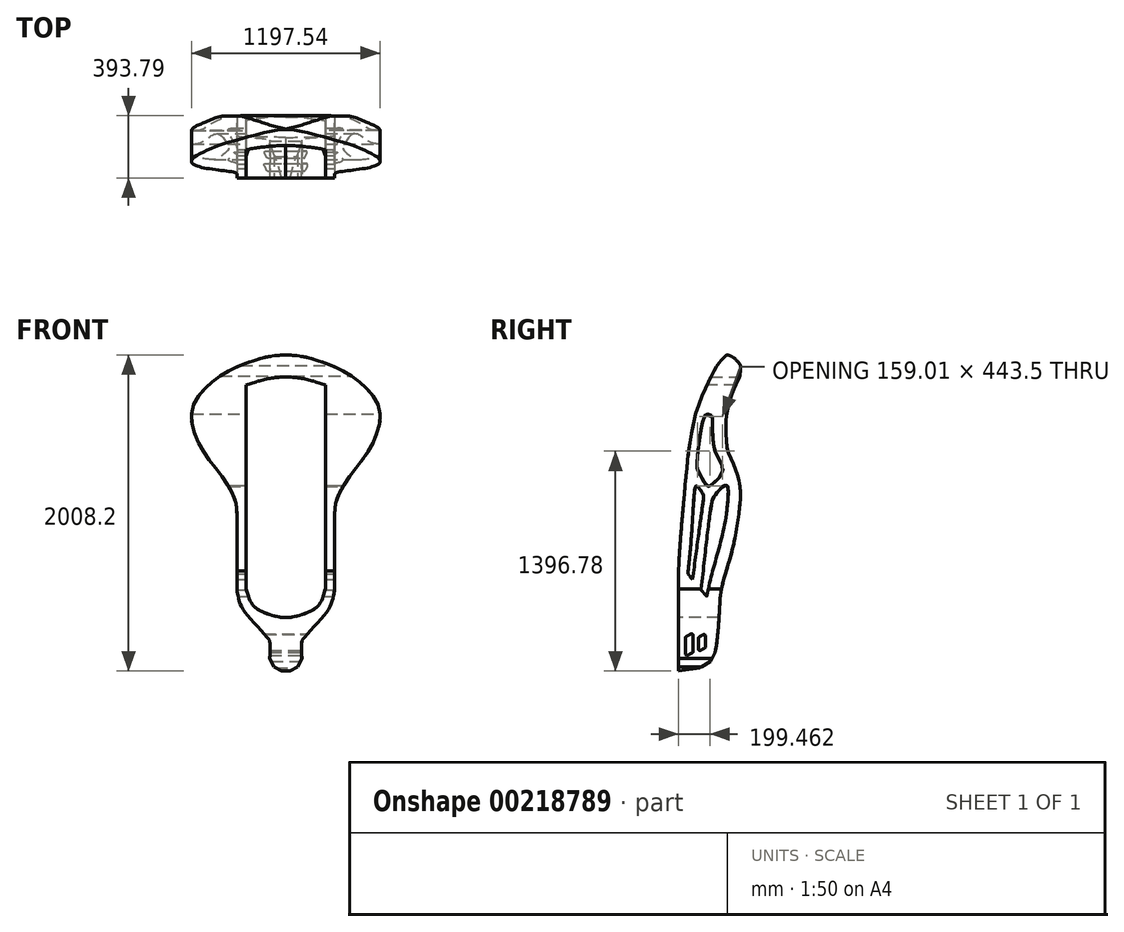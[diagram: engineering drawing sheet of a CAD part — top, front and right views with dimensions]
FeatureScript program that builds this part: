
annotation { "Feature Type Name" : "Feature", "Feature Type Description" : "" }
export const myFeature = defineFeature(function(context is Context, id is Id, definition is map)
    precondition{}
    {
        {
            var Q0;
            Q0=qCreatedBy(makeId("Front.planeOp"),FACE);
            var sketch = newSketch(context, id + "F0", { "sketchPlane" : qUnion([Q0])});
            skLineSegment(sketch, "E0", {"start": v(-255.28, -84.36) * mm, "end": v(252.72, -84.36) * mm});
            skLineSegment(sketch, "E1", {"start": v(0, -829.48) * mm, "end": v(0, 1173.27) * mm});
            skSolve(sketch);
        }
        {
            var Q0;
            Q0=qCreatedBy(makeId("Right.planeOp"),FACE);
            var sketch = newSketch(context, id + "F1", { "sketchPlane" : qUnion([Q0])});
            skLineSegment(sketch, "E2.0", {"start": v(0, -829.48) * mm, "end": v(0, 1173.27) * mm});
            skSolve(sketch);
        }
        {
            var Q0;
            Q0=qCreatedBy(makeId("Front.planeOp"),FACE);
            var sketch = newSketch(context, id + "F2", { "sketchPlane" : qUnion([Q0])});
            skFitSpline(sketch, "E3", {"points": [v(0, 1178.72) * mm, v(-131.61, 1163.15) * mm, v(-387.55, 1062.86) * mm, v(-534.54, 943.54) * mm, v(-586.42, 860.53) * mm, v(-598.52, 786.17) * mm, v(-593.33, 730.83) * mm, v(-536.94, 587.44) * mm, v(-445.29, 459.48) * mm, v(-334.61, 291.74) * mm, v(-310.9, 168.96) * mm], "startDerivative": vector(-1185.5, -55.3) * mm, "endDerivative": vector(0, -1218.83) * mm});
            skLineSegment(sketch, "E4", {"start": v(-310.9, 168.96) * mm, "end": v(-310.9, -308.33) * mm});
            skFitSpline(sketch, "E5", {"points": [v(-310.9, -308.33) * mm, v(-292.5, -393.37) * mm, v(-233.06, -486.5) * mm, v(-109.25, -625.95) * mm, v(-101.61, -641.2) * mm, v(-101.61, -747.96) * mm], "startDerivative": vector(68.26, -452.87) * mm, "endDerivative": vector(-14.07, -627.34) * mm});
            skLineSegment(sketch, "E6", {"start": v(-101.61, -747.96) * mm, "end": v(-75.98, -803.52) * mm});
            skLineSegment(sketch, "E7", {"start": v(-75.98, -803.52) * mm, "end": v(-19.8, -832.39) * mm});
            skLineSegment(sketch, "E8", {"start": v(-19.8, -832.39) * mm, "end": v(0, -832.39) * mm});
            skLineSegment(sketch, "E9", {"start": v(0, 1178.72) * mm, "end": v(0, -832.39) * mm, "construction": true});
            skLineSegment(sketch, "E10.MirrorCS", {"start": v(75.98, -803.52) * mm, "end": v(19.8, -832.39) * mm});
            skLineSegment(sketch, "E11.MirrorCS", {"start": v(101.61, -747.96) * mm, "end": v(75.98, -803.52) * mm});
            skLineSegment(sketch, "E12.MirrorCS", {"start": v(19.8, -832.39) * mm, "end": v(0, -832.39) * mm});
            skFitSpline(sketch, "E13.MirrorCS", {"points": [v(310.9, -308.33) * mm, v(292.5, -393.37) * mm, v(233.06, -486.5) * mm, v(109.25, -625.95) * mm, v(101.61, -641.2) * mm, v(101.61, -747.96) * mm], "startDerivative": vector(-68.26, -452.87) * mm, "endDerivative": vector(14.07, -627.34) * mm});
            skLineSegment(sketch, "E14.MirrorCS", {"start": v(310.9, 168.96) * mm, "end": v(310.9, -308.33) * mm});
            skFitSpline(sketch, "E15.MirrorCS", {"points": [v(0, 1178.72) * mm, v(131.61, 1163.15) * mm, v(387.55, 1062.86) * mm, v(534.54, 943.54) * mm, v(586.42, 860.53) * mm, v(598.52, 786.17) * mm, v(593.33, 730.83) * mm, v(536.94, 587.44) * mm, v(445.29, 459.48) * mm, v(334.61, 291.74) * mm, v(310.9, 168.96) * mm], "startDerivative": vector(1185.5, -55.3) * mm, "endDerivative": vector(0, -1218.83) * mm});
            skSolve(sketch);
        }
        {
            var Q0;
            Q0 = qSketchRegion(id + "F2", true);
            extrude(context, id + "F3", {"entities" : qUnion([Q0]), "oppositeDirection" : true, "depth" : 523.24 * mm});
        }
        {
            var Q0;
            Q0=qCreatedBy(makeId("Right.planeOp"),FACE);
            var sketch = newSketch(context, id + "F4", { "sketchPlane" : qUnion([Q0])});
            skLineSegment(sketch, "E16.0", {"start": v(523.24, 1178.72) * mm, "end": v(0, 1178.72) * mm, "construction": true});
            skLineSegment(sketch, "E17.0", {"start": v(0, -829.48) * mm, "end": v(0, 1173.27) * mm, "construction": true});
            skFitSpline(sketch, "E18", {"points": [v(0, -829.48) * mm, v(0, -194.12) * mm, v(23.27, 143.63) * mm, v(62.09, 547.37) * mm, v(96.06, 753.12) * mm, v(140.7, 898.7) * mm, v(255.63, 1125.36) * mm, v(307.85, 1178.72) * mm], "startDerivative": vector(-39.4, 3171.5) * mm, "endDerivative": vector(647.49, 513.12) * mm});
            skFitSpline(sketch, "E19", {"points": [v(231.85, -711.1) * mm, v(246.25, -618.56) * mm, v(260.64, -421.14) * mm, v(272.98, -301.86) * mm, v(336.73, -75.65) * mm, v(375.8, 123.83) * mm, v(392.26, 269.84) * mm, v(390.2, 337.7) * mm, v(373.75, 417.9) * mm, v(338.79, 506.34) * mm, v(307.85, 586.06) * mm, v(301.76, 738.3) * mm, v(305.26, 807.25) * mm, v(341.33, 935.08) * mm, v(361.45, 984.12) * mm, v(390.27, 1044.51) * mm], "startDerivative": vector(248.18, 1330.22) * mm, "endDerivative": vector(610.21, 1265.5) * mm});
            skFitSpline(sketch, "E20", {"points": [v(307.85, 1178.72) * mm, v(350.06, 1159.99) * mm, v(393.79, 1113) * mm], "startDerivative": vector(77.42, 1.05) * mm, "endDerivative": vector(93.18, -122.51) * mm});
            skLineSegment(sketch, "E21", {"start": v(393.79, 1113) * mm, "end": v(390.27, 1044.51) * mm});
            skLineSegment(sketch, "E22", {"start": v(231.85, -711.1) * mm, "end": v(202.08, -767.87) * mm});
            skLineSegment(sketch, "E23", {"start": v(202.08, -767.87) * mm, "end": v(135.63, -809.16) * mm});
            skLineSegment(sketch, "E24", {"start": v(135.63, -809.16) * mm, "end": v(0, -829.48) * mm});
            skLineSegment(sketch, "E25.bottom", {"start": v(647.82, 1273) * mm, "end": v(-285.83, 1273) * mm});
            skLineSegment(sketch, "E25.top", {"start": v(647.82, -902.76) * mm, "end": v(-285.83, -902.76) * mm});
            skLineSegment(sketch, "E25.left", {"start": v(647.82, 1273) * mm, "end": v(647.82, -902.76) * mm});
            skLineSegment(sketch, "E25.right", {"start": v(-285.83, 1273) * mm, "end": v(-285.83, -902.76) * mm});
            skSolve(sketch);
        }
        {
            var Q0;
            Q0 = qSketchRegion(id + "F4", true);
            extrude(context, id + "F5", {"entities" : qUnion([Q0]), "operationType" : NewBodyOperationType.REMOVE, "endBound" : BoundingType.THROUGH_ALL, "oppositeDirection" : true, "depth" : 25.4 * mm, "hasSecondDirection" : true, "secondDirectionBound" : SecondDirectionBoundingType.THROUGH_ALL, "secondDirectionOppositeDirection" : false, "secondDirectionDepth" : 25.4 * mm});
        }
        {
            var Q0;
            Q0=qCreatedBy(makeId("Front.planeOp"),FACE);
            var sketch = newSketch(context, id + "F6", { "sketchPlane" : qUnion([Q0])});
            skFitSpline(sketch, "E26.0.0", {"points": [v(310.9, 168.96) * mm, v(310.9, 172.92) * mm, v(311.01, 180.84) * mm, v(311.52, 192.71) * mm, v(312.42, 204.58) * mm, v(313.76, 216.32) * mm, v(315.53, 227.96) * mm, v(317.77, 239.47) * mm, v(320.48, 250.86) * mm, v(323.66, 262.14) * mm, v(327.32, 273.28) * mm, v(331.45, 284.3) * mm, v(334.9, 292.49) * mm, v(337.34, 297.9) * mm, v(339, 301.5) * mm, v(341.13, 305.97) * mm, v(343.77, 311.28) * mm, v(347.39, 318.29) * mm, v(353.96, 330.38) * mm, v(363.92, 347.25) * mm, v(376.6, 366.98) * mm, v(389.85, 386.32) * mm, v(403.55, 405.34) * mm, v(422.3, 430.35) * mm, v(441.63, 454.96) * mm, v(461.2, 479.4) * mm, v(475.83, 497.74) * mm, v(487.82, 513.17) * mm, v(497.17, 525.67) * mm, v(504.04, 535.15) * mm, v(509.62, 543.14) * mm, v(513.98, 549.6) * mm, v(517.2, 554.49) * mm, v(520.38, 559.4) * mm, v(524.51, 565.99) * mm, v(529.53, 574.29) * mm, v(535.3, 584.36) * mm, v(540.79, 594.54) * mm, v(546.04, 604.83) * mm, v(552.77, 618.66) * mm, v(560.68, 636.15) * mm, v(569.48, 657.43) * mm, v(576.26, 675.38) * mm, v(581.32, 689.88) * mm, v(584.93, 700.83) * mm, v(588.31, 711.88) * mm, v(591.41, 722.94) * mm, v(594.16, 734.03) * mm, v(596.4, 745.18) * mm, v(598, 756.4) * mm, v(598.64, 765.83) * mm, v(598.8, 773.4) * mm, v(598.75, 779.1) * mm, v(598.59, 784.81) * mm, v(598.34, 790.53) * mm, v(598.02, 796.22) * mm, v(597.48, 803.78) * mm, v(596.58, 813.15) * mm, v(595.1, 824.27) * mm, v(593.19, 835.25) * mm, v(590.76, 846.1) * mm, v(588.26, 855.02) * mm, v(585.92, 862.07) * mm, v(584.3, 866.44) * mm, v(582.93, 869.92) * mm, v(581.85, 872.52) * mm, v(580.74, 875.1) * mm, v(579.2, 878.5) * mm, v(577.19, 882.7) * mm, v(573.79, 889.32) * mm, v(569.22, 897.37) * mm, v(563.27, 906.73) * mm, v(556.93, 915.84) * mm, v(550.23, 924.73) * mm, v(544.4, 931.98) * mm, v(539.6, 937.7) * mm, v(535.95, 941.94) * mm, v(532.24, 946.15) * mm, v(527.24, 951.7) * mm, v(520.9, 958.53) * mm, v(510.5, 969.24) * mm, v(497.12, 982.22) * mm, v(483.2, 994.68) * mm, v(471.76, 1004.34) * mm, v(463.03, 1011.43) * mm, v(455.62, 1017.22) * mm, v(449.62, 1021.77) * mm, v(443.58, 1026.27) * mm, v(435.96, 1031.77) * mm, v(423.63, 1040.35) * mm, v(407.95, 1050.64) * mm, v(388.73, 1062.32) * mm, v(369.1, 1073.34) * mm, v(349.12, 1083.78) * mm, v(328.84, 1093.7) * mm, v(308.28, 1103.15) * mm, v(287.47, 1112.15) * mm, v(269.94, 1119.29) * mm, v(255.8, 1124.78) * mm, v(241.6, 1130.13) * mm, v(223.8, 1136.5) * mm, v(202.35, 1143.68) * mm, v(180.8, 1150.35) * mm, v(159.14, 1156.47) * mm, v(140.96, 1161.06) * mm, v(126.3, 1164.36) * mm, v(111.54, 1167.4) * mm, v(92.9, 1170.7) * mm, v(70.17, 1173.8) * mm, v(47.07, 1176.07) * mm, v(23.64, 1177.61) * mm, v(7.88, 1178.35) * mm, v(0, 1178.72) * mm]});
            skFitSpline(sketch, "E26.0.1", {"points": [v(0, 1178.72) * mm, v(-7.88, 1178.35) * mm, v(-23.64, 1177.61) * mm, v(-47.07, 1176.07) * mm, v(-70.17, 1173.8) * mm, v(-92.9, 1170.7) * mm, v(-111.54, 1167.4) * mm, v(-126.3, 1164.36) * mm, v(-140.96, 1161.06) * mm, v(-159.14, 1156.47) * mm, v(-180.8, 1150.35) * mm, v(-202.35, 1143.68) * mm, v(-223.8, 1136.5) * mm, v(-241.6, 1130.13) * mm, v(-255.8, 1124.78) * mm, v(-269.94, 1119.29) * mm, v(-287.47, 1112.15) * mm, v(-308.28, 1103.15) * mm, v(-328.84, 1093.7) * mm, v(-349.12, 1083.78) * mm, v(-369.1, 1073.34) * mm, v(-388.73, 1062.32) * mm, v(-407.95, 1050.64) * mm, v(-423.63, 1040.35) * mm, v(-435.96, 1031.77) * mm, v(-443.58, 1026.27) * mm, v(-449.62, 1021.77) * mm, v(-455.62, 1017.22) * mm, v(-463.03, 1011.43) * mm, v(-471.76, 1004.34) * mm, v(-483.2, 994.68) * mm, v(-497.12, 982.22) * mm, v(-510.5, 969.24) * mm, v(-520.9, 958.53) * mm, v(-527.24, 951.7) * mm, v(-532.24, 946.15) * mm, v(-535.95, 941.94) * mm, v(-539.6, 937.7) * mm, v(-544.4, 931.98) * mm, v(-550.23, 924.73) * mm, v(-556.93, 915.84) * mm, v(-563.27, 906.73) * mm, v(-569.22, 897.37) * mm, v(-573.79, 889.32) * mm, v(-577.19, 882.7) * mm, v(-579.2, 878.5) * mm, v(-580.74, 875.1) * mm, v(-581.85, 872.52) * mm, v(-582.93, 869.92) * mm, v(-584.3, 866.44) * mm, v(-585.92, 862.07) * mm, v(-588.26, 855.02) * mm, v(-590.76, 846.1) * mm, v(-593.19, 835.25) * mm, v(-595.1, 824.27) * mm, v(-596.58, 813.15) * mm, v(-597.48, 803.78) * mm, v(-598.02, 796.22) * mm, v(-598.34, 790.53) * mm, v(-598.59, 784.81) * mm, v(-598.75, 779.1) * mm, v(-598.8, 773.4) * mm, v(-598.64, 765.83) * mm, v(-598, 756.4) * mm, v(-596.4, 745.18) * mm, v(-594.16, 734.03) * mm, v(-591.41, 722.94) * mm, v(-588.31, 711.88) * mm, v(-584.93, 700.83) * mm, v(-581.32, 689.88) * mm, v(-576.26, 675.38) * mm, v(-569.48, 657.43) * mm, v(-560.68, 636.15) * mm, v(-552.77, 618.66) * mm, v(-546.04, 604.83) * mm, v(-540.79, 594.54) * mm, v(-535.3, 584.36) * mm, v(-529.53, 574.29) * mm, v(-524.51, 565.99) * mm, v(-520.38, 559.4) * mm, v(-517.2, 554.49) * mm, v(-513.98, 549.6) * mm, v(-509.62, 543.14) * mm, v(-504.04, 535.15) * mm, v(-497.17, 525.67) * mm, v(-487.82, 513.17) * mm, v(-475.83, 497.74) * mm, v(-461.2, 479.4) * mm, v(-441.63, 454.96) * mm, v(-422.3, 430.35) * mm, v(-403.55, 405.34) * mm, v(-389.85, 386.32) * mm, v(-376.6, 366.98) * mm, v(-363.92, 347.25) * mm, v(-353.96, 330.38) * mm, v(-347.39, 318.29) * mm, v(-343.77, 311.28) * mm, v(-341.13, 305.97) * mm, v(-339, 301.5) * mm, v(-337.34, 297.9) * mm, v(-334.9, 292.49) * mm, v(-331.45, 284.3) * mm, v(-327.32, 273.28) * mm, v(-323.66, 262.14) * mm, v(-320.48, 250.86) * mm, v(-317.77, 239.47) * mm, v(-315.53, 227.96) * mm, v(-313.76, 216.32) * mm, v(-312.42, 204.58) * mm, v(-311.52, 192.71) * mm, v(-311.01, 180.84) * mm, v(-310.9, 172.92) * mm, v(-310.9, 168.96) * mm]});
            skFitSpline(sketch, "E26.0.2", {"points": [v(-310.9, 1178.72) * mm, v(-310.9, 1165.88) * mm, v(-310.9, 1129.35) * mm, v(-310.9, 894.02) * mm, v(-310.9, 753.1) * mm, v(-310.9, 541.34) * mm, v(-310.9, 129.24) * mm, v(-310.9, -197.5) * mm, v(-310.9, -597.98) * mm, v(-310.9, -829.48) * mm]});
            skFitSpline(sketch, "E26.0.4", {"points": [v(310.9, 1178.72) * mm, v(310.9, 1165.88) * mm, v(310.9, 1129.35) * mm, v(310.9, 894.02) * mm, v(310.9, 753.1) * mm, v(310.9, 541.34) * mm, v(310.9, 129.24) * mm, v(310.9, -197.5) * mm, v(310.9, -597.98) * mm, v(310.9, -829.48) * mm]});
            skLineSegment(sketch, "E26.1.0", {"start": v(-25.46, -829.48) * mm, "end": v(25.46, -829.48) * mm});
            skLineSegment(sketch, "E26.1.1", {"start": v(25.46, -829.48) * mm, "end": v(75.98, -803.52) * mm});
            skLineSegment(sketch, "E26.1.2", {"start": v(75.98, -803.52) * mm, "end": v(101.61, -747.96) * mm});
            skFitSpline(sketch, "E26.1.3", {"points": [v(101.61, -747.96) * mm, v(100.6, -702.9) * mm, v(99.19, -639.84) * mm, v(107.99, -625.42) * mm, v(242.04, -482.32) * mm, v(297.07, -400.14) * mm, v(306.48, -337.69) * mm, v(310.9, -308.33) * mm]});
            skLineSegment(sketch, "E26.1.4", {"start": v(310.9, -308.33) * mm, "end": v(310.9, -194.12) * mm});
            skLineSegment(sketch, "E26.1.6", {"start": v(-310.9, -194.12) * mm, "end": v(-310.9, -308.33) * mm});
            skFitSpline(sketch, "E26.1.7", {"points": [v(-310.9, -308.33) * mm, v(-306.48, -337.69) * mm, v(-297.07, -400.14) * mm, v(-242.04, -482.32) * mm, v(-107.99, -625.42) * mm, v(-99.19, -639.84) * mm, v(-100.6, -702.9) * mm, v(-101.61, -747.96) * mm]});
            skLineSegment(sketch, "E26.1.8", {"start": v(-101.61, -747.96) * mm, "end": v(-75.98, -803.52) * mm});
            skLineSegment(sketch, "E26.1.9", {"start": v(-75.98, -803.52) * mm, "end": v(-25.46, -829.48) * mm});
            skFitSpline(sketch, "E27.0", {"points": [v(252.49, 1178.72) * mm, v(252.49, 1176.05) * mm, v(252.49, 1170.7) * mm, v(252.49, 1161.88) * mm, v(252.49, 1153.2) * mm, v(252.49, 1145.03) * mm, v(252.49, 1138.21) * mm, v(252.49, 1131.86) * mm, v(252.49, 1126.33) * mm, v(252.49, 1120.47) * mm, v(252.49, 1112.57) * mm, v(252.49, 1102.24) * mm, v(252.49, 1091.15) * mm, v(252.49, 1075.45) * mm, v(252.49, 1054.35) * mm, v(252.49, 1027.31) * mm, v(252.49, 999.24) * mm, v(252.49, 970.82) * mm, v(252.49, 947.39) * mm, v(252.49, 929.14) * mm, v(252.49, 915.78) * mm, v(252.49, 905) * mm, v(252.49, 896.62) * mm, v(252.49, 888.42) * mm, v(252.49, 878.47) * mm, v(252.49, 866.97) * mm, v(252.49, 855.86) * mm, v(252.49, 841.48) * mm, v(252.49, 824.18) * mm, v(252.49, 804.08) * mm, v(252.49, 787.52) * mm, v(252.49, 774.16) * mm, v(252.49, 764.04) * mm, v(252.49, 753.75) * mm, v(252.49, 743.24) * mm, v(252.49, 732.5) * mm, v(252.49, 717.85) * mm, v(252.49, 698.88) * mm, v(252.49, 674.93) * mm, v(252.49, 649.7) * mm, v(252.49, 623.06) * mm, v(252.49, 599.58) * mm, v(252.49, 579.97) * mm, v(252.49, 564.84) * mm, v(252.49, 549.27) * mm, v(252.49, 533.23) * mm, v(252.49, 516.77) * mm, v(252.49, 494.3) * mm, v(252.49, 465.33) * mm, v(252.49, 429.42) * mm, v(252.49, 392.65) * mm, v(252.49, 355.3) * mm, v(252.49, 317.67) * mm, v(252.49, 280.02) * mm, v(252.49, 242.64) * mm, v(252.49, 211.96) * mm, v(252.49, 187.83) * mm, v(252.49, 169.99) * mm, v(252.49, 152.41) * mm, v(252.49, 135.17) * mm, v(252.49, 118.24) * mm, v(252.49, 96.04) * mm, v(252.49, 68.88) * mm, v(252.49, 36.94) * mm, v(252.49, -5.2) * mm, v(252.49, -57.8) * mm, v(252.49, -123.23) * mm, v(252.49, -193.46) * mm, v(252.49, -270.92) * mm, v(252.49, -354.56) * mm, v(252.49, -443.36) * mm, v(252.49, -536.28) * mm, v(252.49, -632.3) * mm, v(252.49, -730.37) * mm, v(252.49, -796.44) * mm, v(252.49, -829.48) * mm]});
            skLineSegment(sketch, "E27.1", {"start": v(252.49, -303.95) * mm, "end": v(252.49, -194.12) * mm});
            skFitSpline(sketch, "E27.2", {"points": [v(-253.14, -299.62) * mm, v(-252.43, -304.34) * mm, v(-251.04, -313.59) * mm, v(-248.9, -326.83) * mm, v(-246.64, -339.34) * mm, v(-244.16, -351.04) * mm, v(-241.87, -360.01) * mm, v(-239.89, -366.7) * mm, v(-238.33, -371.44) * mm, v(-236.7, -375.92) * mm, v(-234.93, -380.29) * mm, v(-233, -384.62) * mm, v(-230.88, -388.98) * mm, v(-228.53, -393.45) * mm, v(-225.03, -399.6) * mm, v(-219.88, -407.83) * mm, v(-213.46, -417.01) * mm, v(-207.47, -425.05) * mm, v(-202.53, -431.45) * mm, v(-197.12, -438.24) * mm, v(-192.22, -444.24) * mm, v(-188.05, -449.27) * mm, v(-183.72, -454.44) * mm, v(-178.01, -461.17) * mm, v(-170.8, -469.55) * mm, v(-160.77, -481.06) * mm, v(-147.7, -495.86) * mm, v(-131.75, -513.7) * mm, v(-118.69, -528.15) * mm, v(-108.67, -539.2) * mm, v(-101.43, -547.18) * mm, v(-94.55, -554.77) * mm, v(-88.07, -561.91) * mm, v(-82.07, -568.55) * mm, v(-77.52, -573.61) * mm, v(-74.16, -577.37) * mm, v(-71.79, -580.04) * mm, v(-69.57, -582.55) * mm, v(-67.84, -584.52) * mm, v(-66.52, -586.03) * mm, v(-65.73, -586.95) * mm, v(-65.11, -587.67) * mm, v(-64.5, -588.38) * mm, v(-63.73, -589.3) * mm, v(-62.77, -590.45) * mm, v(-61.41, -592.1) * mm, v(-59.56, -594.43) * mm, v(-57.04, -597.86) * mm, v(-54.26, -602.1) * mm, v(-51.42, -607.18) * mm, v(-48.83, -612.85) * mm, v(-47.11, -617.68) * mm, v(-46.04, -621.36) * mm, v(-45.38, -623.98) * mm, v(-44.84, -626.43) * mm, v(-44.42, -628.7) * mm, v(-44.08, -630.78) * mm, v(-43.85, -632.37) * mm, v(-43.7, -633.57) * mm, v(-43.59, -634.43) * mm, v(-43.49, -635.27) * mm, v(-43.37, -636.39) * mm, v(-43.23, -637.76) * mm, v(-43.04, -639.93) * mm, v(-42.83, -642.61) * mm, v(-42.64, -645.86) * mm, v(-42.47, -649.16) * mm, v(-42.3, -653.68) * mm, v(-42.15, -659.57) * mm, v(-42.05, -667.07) * mm, v(-42.02, -675) * mm, v(-42.04, -683.35) * mm, v(-42.12, -692.08) * mm, v(-42.24, -701.12) * mm, v(-42.44, -713.55) * mm, v(-42.77, -729.62) * mm, v(-43.06, -742.74) * mm, v(-43.2, -749.27) * mm]});
            skLineSegment(sketch, "E27.3", {"start": v(-252.49, -194.12) * mm, "end": v(-252.49, -303.95) * mm});
            skFitSpline(sketch, "E27.4", {"points": [v(-252.49, 1178.72) * mm, v(-252.49, 1176.05) * mm, v(-252.49, 1170.7) * mm, v(-252.49, 1161.88) * mm, v(-252.49, 1153.2) * mm, v(-252.49, 1145.03) * mm, v(-252.49, 1138.21) * mm, v(-252.49, 1131.86) * mm, v(-252.49, 1126.33) * mm, v(-252.49, 1120.47) * mm, v(-252.49, 1112.57) * mm, v(-252.49, 1102.24) * mm, v(-252.49, 1091.15) * mm, v(-252.49, 1075.45) * mm, v(-252.49, 1054.35) * mm, v(-252.49, 1027.31) * mm, v(-252.49, 999.24) * mm, v(-252.49, 970.82) * mm, v(-252.49, 947.39) * mm, v(-252.49, 929.14) * mm, v(-252.49, 915.78) * mm, v(-252.49, 905) * mm, v(-252.49, 896.62) * mm, v(-252.49, 888.42) * mm, v(-252.49, 878.47) * mm, v(-252.49, 866.97) * mm, v(-252.49, 855.86) * mm, v(-252.49, 841.48) * mm, v(-252.49, 824.18) * mm, v(-252.49, 804.08) * mm, v(-252.49, 787.52) * mm, v(-252.49, 774.16) * mm, v(-252.49, 764.04) * mm, v(-252.49, 753.75) * mm, v(-252.49, 743.24) * mm, v(-252.49, 732.5) * mm, v(-252.49, 717.85) * mm, v(-252.49, 698.88) * mm, v(-252.49, 674.93) * mm, v(-252.49, 649.7) * mm, v(-252.49, 623.06) * mm, v(-252.49, 599.58) * mm, v(-252.49, 579.97) * mm, v(-252.49, 564.84) * mm, v(-252.49, 549.27) * mm, v(-252.49, 533.23) * mm, v(-252.49, 516.77) * mm, v(-252.49, 494.3) * mm, v(-252.49, 465.33) * mm, v(-252.49, 429.42) * mm, v(-252.49, 392.65) * mm, v(-252.49, 355.3) * mm, v(-252.49, 317.67) * mm, v(-252.49, 280.02) * mm, v(-252.49, 242.64) * mm, v(-252.49, 211.96) * mm, v(-252.49, 187.83) * mm, v(-252.49, 169.99) * mm, v(-252.49, 152.41) * mm, v(-252.49, 135.17) * mm, v(-252.49, 118.24) * mm, v(-252.49, 96.04) * mm, v(-252.49, 68.88) * mm, v(-252.49, 36.94) * mm, v(-252.49, -5.2) * mm, v(-252.49, -57.8) * mm, v(-252.49, -123.23) * mm, v(-252.49, -193.46) * mm, v(-252.49, -270.92) * mm, v(-252.49, -354.56) * mm, v(-252.49, -443.36) * mm, v(-252.49, -536.28) * mm, v(-252.49, -632.3) * mm, v(-252.49, -730.37) * mm, v(-252.49, -796.44) * mm, v(-252.49, -829.48) * mm]});
            skFitSpline(sketch, "E27.5", {"points": [v(2.72, 1120.36) * mm, v(-1.21, 1120.18) * mm, v(-7.05, 1119.9) * mm, v(-14.68, 1119.52) * mm, v(-20.33, 1119.22) * mm, v(-25.9, 1118.89) * mm, v(-31.42, 1118.53) * mm, v(-36.87, 1118.15) * mm, v(-42.26, 1117.73) * mm, v(-47.59, 1117.27) * mm, v(-52.88, 1116.77) * mm, v(-58.13, 1116.23) * mm, v(-63.33, 1115.65) * mm, v(-68.49, 1115.02) * mm, v(-73.62, 1114.34) * mm, v(-78.73, 1113.62) * mm, v(-83.81, 1112.85) * mm, v(-88.87, 1112.03) * mm, v(-95.6, 1110.88) * mm, v(-102.29, 1109.63) * mm, v(-108.96, 1108.29) * mm, v(-113.95, 1107.23) * mm, v(-118.94, 1106.13) * mm, v(-125.6, 1104.6) * mm, v(-132.29, 1102.97) * mm, v(-138.98, 1101.26) * mm, v(-144.02, 1099.93) * mm, v(-149.06, 1098.57) * mm, v(-155.79, 1096.7) * mm, v(-167.57, 1093.29) * mm, v(-184.44, 1088.07) * mm, v(-201.3, 1082.43) * mm, v(-214.77, 1077.69) * mm, v(-224.86, 1074) * mm, v(-234.94, 1070.21) * mm, v(-244.96, 1066.32) * mm, v(-254.93, 1062.32) * mm, v(-268.14, 1056.86) * mm, v(-284.5, 1049.79) * mm, v(-303.81, 1040.91) * mm, v(-319.6, 1033.18) * mm, v(-332.03, 1026.8) * mm, v(-341.23, 1021.9) * mm, v(-348.78, 1017.73) * mm, v(-354.76, 1014.34) * mm, v(-359.2, 1011.77) * mm, v(-363.6, 1009.17) * mm, v(-369.46, 1005.65) * mm, v(-376.7, 1001.16) * mm, v(-385.3, 995.63) * mm, v(-393.78, 989.95) * mm, v(-402.17, 984.12) * mm, v(-409.06, 979.13) * mm, v(-414.52, 975.07) * mm, v(-419.95, 970.95) * mm, v(-426.63, 965.73) * mm, v(-434.5, 959.34) * mm, v(-444.8, 950.64) * mm, v(-457.3, 939.46) * mm, v(-469.27, 927.85) * mm, v(-477.37, 919.5) * mm, v(-481.91, 914.66) * mm, v(-485.28, 911) * mm, v(-488.6, 907.3) * mm, v(-491.89, 903.58) * mm, v(-495.09, 899.85) * mm, v(-498.2, 896.15) * mm, v(-501.2, 892.47) * mm, v(-505.08, 887.57) * mm, v(-509.64, 881.51) * mm, v(-514.65, 874.32) * mm, v(-519.15, 867.22) * mm, v(-522.46, 861.37) * mm, v(-524.86, 856.71) * mm, v(-526.25, 853.8) * mm, v(-527.3, 851.48) * mm, v(-528.06, 849.73) * mm, v(-528.78, 847.98) * mm, v(-529.47, 846.24) * mm, v(-530.13, 844.5) * mm, v(-530.75, 842.77) * mm, v(-531.34, 841.03) * mm, v(-532.1, 838.66) * mm, v(-532.83, 836.23) * mm, v(-533.52, 833.72) * mm, v(-534.18, 831.17) * mm, v(-534.96, 827.9) * mm, v(-536.1, 822.48) * mm, v(-537.34, 815.44) * mm, v(-538.33, 808.04) * mm, v(-538.97, 801.94) * mm, v(-539.3, 798.05) * mm, v(-539.55, 794.89) * mm, v(-539.7, 792.5) * mm, v(-539.85, 790.09) * mm, v(-539.96, 788.05) * mm, v(-540.04, 786.42) * mm, v(-540.1, 785.19) * mm, v(-540.14, 783.96) * mm, v(-540.19, 782.73) * mm, v(-540.23, 781.52) * mm, v(-540.28, 779.94) * mm, v(-540.32, 778.03) * mm, v(-540.35, 775.84) * mm, v(-540.35, 773.74) * mm, v(-540.33, 772.07) * mm, v(-540.3, 770.77) * mm, v(-540.27, 769.82) * mm, v(-540.23, 768.9) * mm, v(-540.17, 767.65) * mm, v(-540.08, 766.12) * mm, v(-539.96, 764.6) * mm, v(-539.85, 763.4) * mm, v(-539.76, 762.51) * mm, v(-539.66, 761.62) * mm, v(-539.52, 760.4) * mm, v(-539.32, 758.88) * mm, v(-539.04, 757) * mm, v(-538.73, 755.07) * mm, v(-538.37, 753.1) * mm, v(-537.85, 750.4) * mm, v(-537.25, 747.59) * mm, v(-536.58, 744.67) * mm, v(-536.04, 742.44) * mm, v(-535.47, 740.17) * mm, v(-534.87, 737.85) * mm, v(-534.24, 735.5) * mm, v(-533.59, 733.13) * mm, v(-532.91, 730.74) * mm, v(-531.98, 727.52) * mm, v(-530.76, 723.46) * mm, v(-528.71, 716.9) * mm, v(-526, 708.66) * mm, v(-523.11, 700.39) * mm, v(-520.71, 693.78) * mm, v(-518.87, 688.83) * mm, v(-516.98, 683.89) * mm, v(-515.05, 678.96) * mm, v(-513.09, 674.04) * mm, v(-511.08, 669.14) * mm, v(-509.04, 664.27) * mm, v(-506.96, 659.4) * mm, v(-504.85, 654.58) * mm, v(-502.7, 649.77) * mm, v(-500.5, 645) * mm, v(-497.54, 638.68) * mm, v(-494.5, 632.43) * mm, v(-491.4, 626.28) * mm, v(-489.03, 621.71) * mm, v(-487.03, 617.96) * mm, v(-485.41, 614.97) * mm, v(-484.19, 612.75) * mm, v(-482.95, 610.54) * mm, v(-481.27, 607.6) * mm, v(-479.14, 603.92) * mm, v(-476.52, 599.52) * mm, v(-473.84, 595.15) * mm, v(-471.1, 590.78) * mm, v(-468.28, 586.41) * mm, v(-465.4, 582.06) * mm, v(-461.49, 576.26) * mm, v(-454.42, 566.13) * mm, v(-445.86, 554.52) * mm, v(-436.86, 542.8) * mm, v(-429.92, 533.92) * mm, v(-422.81, 524.96) * mm, v(-416.78, 517.4) * mm, v(-411.9, 511.3) * mm, v(-408.23, 506.71) * mm, v(-404.54, 502.09) * mm, v(-400.83, 497.44) * mm, v(-397.12, 492.76) * mm, v(-392.16, 486.5) * mm, v(-385.98, 478.63) * mm, v(-378.56, 469.1) * mm, v(-371.18, 459.47) * mm, v(-363.83, 449.75) * mm, v(-354.1, 436.64) * mm, v(-344.48, 423.3) * mm, v(-335.01, 409.65) * mm, v(-329.17, 400.98) * mm, v(-324.55, 393.95) * mm, v(-321.1, 388.63) * mm, v(-317.69, 383.25) * mm, v(-314.3, 377.82) * mm, v(-310.95, 372.33) * mm, v(-307.63, 366.76) * mm, v(-304.35, 361.12) * mm, v(-301.11, 355.4) * mm, v(-297.92, 349.6) * mm, v(-294.77, 343.7) * mm, v(-291.67, 337.7) * mm, v(-288.62, 331.58) * mm, v(-286.13, 326.37) * mm, v(-284.18, 322.14) * mm, v(-282.74, 318.93) * mm, v(-281.32, 315.7) * mm, v(-279.93, 312.45) * mm, v(-278.57, 309.18) * mm, v(-276.8, 304.8) * mm, v(-274.67, 299.29) * mm, v(-272.26, 292.63) * mm, v(-269.98, 285.93) * mm, v(-267.13, 276.92) * mm, v(-263.92, 265.57) * mm, v(-260.65, 251.8) * mm, v(-257.96, 237.93) * mm, v(-256.18, 226.33) * mm, v(-255.04, 217.04) * mm, v(-254.07, 207.74) * mm, v(-253.19, 196.15) * mm, v(-252.6, 182.43) * mm, v(-252.49, 173.42) * mm, v(-252.49, 168.96) * mm]});
            skLineSegment(sketch, "E27.6", {"start": v(-42.9, -735.75) * mm, "end": v(-31.37, -760.76) * mm});
            skLineSegment(sketch, "E27.7", {"start": v(-31.37, -760.76) * mm, "end": v(-11.33, -771.06) * mm});
            skFitSpline(sketch, "E27.8", {"points": [v(252.49, 168.96) * mm, v(252.49, 173.42) * mm, v(252.6, 182.43) * mm, v(253.19, 196.15) * mm, v(254.07, 207.74) * mm, v(255.04, 217.04) * mm, v(256.18, 226.33) * mm, v(257.96, 237.93) * mm, v(260.65, 251.8) * mm, v(263.92, 265.57) * mm, v(267.13, 276.92) * mm, v(269.98, 285.93) * mm, v(272.26, 292.63) * mm, v(274.67, 299.29) * mm, v(276.8, 304.8) * mm, v(278.57, 309.18) * mm, v(279.93, 312.45) * mm, v(281.32, 315.7) * mm, v(282.74, 318.93) * mm, v(284.18, 322.14) * mm, v(286.13, 326.37) * mm, v(288.62, 331.58) * mm, v(291.67, 337.7) * mm, v(294.77, 343.7) * mm, v(297.92, 349.6) * mm, v(301.11, 355.4) * mm, v(304.35, 361.12) * mm, v(307.63, 366.76) * mm, v(310.95, 372.33) * mm, v(314.3, 377.82) * mm, v(317.69, 383.25) * mm, v(321.1, 388.63) * mm, v(324.55, 393.95) * mm, v(329.17, 400.98) * mm, v(335.01, 409.65) * mm, v(344.48, 423.3) * mm, v(354.1, 436.64) * mm, v(363.83, 449.75) * mm, v(371.18, 459.47) * mm, v(378.56, 469.1) * mm, v(385.98, 478.63) * mm, v(392.16, 486.5) * mm, v(397.12, 492.76) * mm, v(400.83, 497.44) * mm, v(404.54, 502.09) * mm, v(408.23, 506.71) * mm, v(411.9, 511.3) * mm, v(416.78, 517.4) * mm, v(422.81, 524.96) * mm, v(429.92, 533.92) * mm, v(436.86, 542.8) * mm, v(445.86, 554.52) * mm, v(454.42, 566.13) * mm, v(461.49, 576.26) * mm, v(465.4, 582.06) * mm, v(468.28, 586.41) * mm, v(471.1, 590.78) * mm, v(473.84, 595.15) * mm, v(476.52, 599.52) * mm, v(479.14, 603.92) * mm, v(481.27, 607.6) * mm, v(482.95, 610.54) * mm, v(484.19, 612.75) * mm, v(485.41, 614.97) * mm, v(487.03, 617.96) * mm, v(489.03, 621.71) * mm, v(491.4, 626.28) * mm, v(494.5, 632.43) * mm, v(497.54, 638.68) * mm, v(500.5, 645) * mm, v(502.7, 649.77) * mm, v(504.85, 654.58) * mm, v(506.96, 659.4) * mm, v(509.04, 664.27) * mm, v(511.08, 669.14) * mm, v(513.09, 674.04) * mm, v(515.05, 678.96) * mm, v(516.98, 683.89) * mm, v(518.87, 688.83) * mm, v(520.71, 693.78) * mm, v(523.11, 700.39) * mm, v(526, 708.66) * mm, v(528.71, 716.9) * mm, v(530.76, 723.46) * mm, v(531.98, 727.52) * mm, v(532.91, 730.74) * mm, v(533.59, 733.13) * mm, v(534.24, 735.5) * mm, v(534.87, 737.85) * mm, v(535.47, 740.17) * mm, v(536.04, 742.44) * mm, v(536.58, 744.67) * mm, v(537.25, 747.59) * mm, v(537.85, 750.4) * mm, v(538.37, 753.1) * mm, v(538.73, 755.07) * mm, v(539.04, 757) * mm, v(539.32, 758.88) * mm, v(539.52, 760.4) * mm, v(539.66, 761.62) * mm, v(539.76, 762.51) * mm, v(539.85, 763.4) * mm, v(539.96, 764.6) * mm, v(540.08, 766.12) * mm, v(540.17, 767.65) * mm, v(540.23, 768.9) * mm, v(540.27, 769.82) * mm, v(540.3, 770.77) * mm, v(540.33, 772.07) * mm, v(540.35, 773.74) * mm, v(540.35, 775.84) * mm, v(540.32, 778.03) * mm, v(540.28, 779.94) * mm, v(540.23, 781.52) * mm, v(540.19, 782.73) * mm, v(540.14, 783.96) * mm, v(540.1, 785.19) * mm, v(540.04, 786.42) * mm, v(539.96, 788.05) * mm, v(539.85, 790.09) * mm, v(539.7, 792.5) * mm, v(539.55, 794.89) * mm, v(539.3, 798.05) * mm, v(538.97, 801.94) * mm, v(538.33, 808.04) * mm, v(537.34, 815.44) * mm, v(536.1, 822.48) * mm, v(534.96, 827.9) * mm, v(534.18, 831.17) * mm, v(533.52, 833.72) * mm, v(532.83, 836.23) * mm, v(532.1, 838.66) * mm, v(531.34, 841.03) * mm, v(530.75, 842.77) * mm, v(530.13, 844.5) * mm, v(529.47, 846.24) * mm, v(528.78, 847.98) * mm, v(528.06, 849.73) * mm, v(527.3, 851.48) * mm, v(526.25, 853.8) * mm, v(524.86, 856.71) * mm, v(522.46, 861.37) * mm, v(519.15, 867.22) * mm, v(514.65, 874.32) * mm, v(509.64, 881.51) * mm, v(505.08, 887.57) * mm, v(501.2, 892.47) * mm, v(498.2, 896.15) * mm, v(495.09, 899.85) * mm, v(491.89, 903.58) * mm, v(488.6, 907.3) * mm, v(485.28, 911) * mm, v(481.91, 914.66) * mm, v(477.37, 919.5) * mm, v(469.27, 927.85) * mm, v(457.3, 939.46) * mm, v(444.8, 950.64) * mm, v(434.5, 959.34) * mm, v(426.63, 965.73) * mm, v(419.95, 970.95) * mm, v(414.52, 975.07) * mm, v(409.06, 979.13) * mm, v(402.17, 984.12) * mm, v(393.78, 989.95) * mm, v(385.3, 995.63) * mm, v(376.7, 1001.16) * mm, v(369.46, 1005.65) * mm, v(363.6, 1009.17) * mm, v(359.2, 1011.77) * mm, v(354.76, 1014.34) * mm, v(348.78, 1017.73) * mm, v(341.23, 1021.9) * mm, v(332.03, 1026.8) * mm, v(319.6, 1033.18) * mm, v(303.81, 1040.91) * mm, v(284.5, 1049.79) * mm, v(268.14, 1056.86) * mm, v(254.93, 1062.32) * mm, v(244.96, 1066.32) * mm, v(234.94, 1070.21) * mm, v(224.86, 1074) * mm, v(214.77, 1077.69) * mm, v(201.3, 1082.43) * mm, v(184.44, 1088.07) * mm, v(167.57, 1093.29) * mm, v(155.79, 1096.7) * mm, v(149.06, 1098.57) * mm, v(144.02, 1099.93) * mm, v(138.98, 1101.26) * mm, v(132.29, 1102.97) * mm, v(125.6, 1104.6) * mm, v(118.94, 1106.13) * mm, v(113.95, 1107.23) * mm, v(108.96, 1108.29) * mm, v(102.29, 1109.63) * mm, v(95.6, 1110.88) * mm, v(88.87, 1112.03) * mm, v(83.81, 1112.85) * mm, v(78.73, 1113.62) * mm, v(73.62, 1114.34) * mm, v(68.49, 1115.02) * mm, v(63.33, 1115.65) * mm, v(58.13, 1116.23) * mm, v(52.88, 1116.77) * mm, v(47.59, 1117.27) * mm, v(42.26, 1117.73) * mm, v(36.87, 1118.15) * mm, v(31.42, 1118.53) * mm, v(25.9, 1118.89) * mm, v(20.33, 1119.22) * mm, v(14.68, 1119.52) * mm, v(7.05, 1119.9) * mm, v(1.21, 1120.18) * mm, v(-2.72, 1120.36) * mm]});
            skLineSegment(sketch, "E27.9", {"start": v(-11.33, -771.06) * mm, "end": v(11.33, -771.06) * mm});
            skLineSegment(sketch, "E27.10", {"start": v(11.33, -771.06) * mm, "end": v(31.37, -760.76) * mm});
            skLineSegment(sketch, "E27.11", {"start": v(31.37, -760.76) * mm, "end": v(42.9, -735.75) * mm});
            skFitSpline(sketch, "E27.12", {"points": [v(43.2, -749.27) * mm, v(43.06, -742.74) * mm, v(42.77, -729.62) * mm, v(42.44, -713.55) * mm, v(42.24, -701.12) * mm, v(42.12, -692.08) * mm, v(42.04, -683.35) * mm, v(42.02, -675) * mm, v(42.05, -667.07) * mm, v(42.15, -659.57) * mm, v(42.3, -653.68) * mm, v(42.47, -649.16) * mm, v(42.64, -645.86) * mm, v(42.83, -642.61) * mm, v(43.04, -639.93) * mm, v(43.23, -637.76) * mm, v(43.37, -636.39) * mm, v(43.49, -635.27) * mm, v(43.59, -634.43) * mm, v(43.7, -633.57) * mm, v(43.85, -632.37) * mm, v(44.08, -630.78) * mm, v(44.42, -628.7) * mm, v(44.84, -626.43) * mm, v(45.38, -623.98) * mm, v(46.04, -621.36) * mm, v(47.11, -617.68) * mm, v(48.83, -612.85) * mm, v(51.42, -607.18) * mm, v(54.26, -602.1) * mm, v(57.04, -597.86) * mm, v(59.56, -594.43) * mm, v(61.41, -592.1) * mm, v(62.77, -590.45) * mm, v(63.73, -589.3) * mm, v(64.5, -588.38) * mm, v(65.11, -587.67) * mm, v(65.73, -586.95) * mm, v(66.52, -586.03) * mm, v(67.84, -584.52) * mm, v(69.57, -582.55) * mm, v(71.79, -580.04) * mm, v(74.16, -577.37) * mm, v(77.52, -573.61) * mm, v(82.07, -568.55) * mm, v(88.07, -561.91) * mm, v(94.55, -554.77) * mm, v(101.43, -547.18) * mm, v(108.67, -539.2) * mm, v(118.69, -528.15) * mm, v(131.75, -513.7) * mm, v(147.7, -495.86) * mm, v(160.77, -481.06) * mm, v(170.8, -469.55) * mm, v(178.01, -461.17) * mm, v(183.72, -454.44) * mm, v(188.05, -449.27) * mm, v(192.22, -444.24) * mm, v(197.12, -438.24) * mm, v(202.53, -431.45) * mm, v(207.47, -425.05) * mm, v(213.46, -417.01) * mm, v(219.88, -407.83) * mm, v(225.03, -399.6) * mm, v(228.53, -393.45) * mm, v(230.88, -388.98) * mm, v(233, -384.62) * mm, v(234.93, -380.29) * mm, v(236.7, -375.92) * mm, v(238.33, -371.44) * mm, v(239.89, -366.7) * mm, v(241.87, -360.01) * mm, v(244.16, -351.04) * mm, v(246.64, -339.34) * mm, v(248.9, -326.83) * mm, v(251.04, -313.59) * mm, v(252.43, -304.34) * mm, v(253.14, -299.62) * mm]});
            skFitSpline(sketch, "E28", {"points": [v(-533.6, 733.18) * mm, v(-538.35, 807.6) * mm, v(-445.42, 899.69) * mm, v(-126.67, 1025.13) * mm, v(0, 1037.47) * mm], "startDerivative": vector(-100.12, 437.17) * mm, "endDerivative": vector(474.07, -1.36) * mm});
            skFitSpline(sketch, "E29", {"points": [v(-252.49, -303.95) * mm, v(-214.34, -403.54) * mm, v(-149.63, -452.26) * mm, v(-45.66, -485.7) * mm, v(0, -489.34) * mm], "startDerivative": vector(108.5, -392.67) * mm, "endDerivative": vector(217.04, -1.44) * mm});
            skLineSegment(sketch, "E30.0", {"start": v(0, -829.48) * mm, "end": v(0, 1173.27) * mm, "construction": true});
            skFitSpline(sketch, "E31.MirrorCS", {"points": [v(252.49, -303.95) * mm, v(214.34, -403.54) * mm, v(149.63, -452.26) * mm, v(45.66, -485.7) * mm, v(0, -489.34) * mm], "startDerivative": vector(-108.5, -392.67) * mm, "endDerivative": vector(-217.04, -1.44) * mm});
            skFitSpline(sketch, "E32.MirrorCS", {"points": [v(533.6, 733.18) * mm, v(538.35, 807.6) * mm, v(445.42, 899.69) * mm, v(126.67, 1025.13) * mm, v(0, 1037.47) * mm], "startDerivative": vector(100.12, 437.17) * mm, "endDerivative": vector(-474.07, -1.36) * mm});
            skSolve(sketch);
        }
        {
            var Q0;
            {var subQ14=sQuery(id+"F6.wireOp",EDGE,"E27.0");Q0=makeQuery(id+"F6.imprint","IMPRINT",FACE,{"disambiguationData":[TD([[makeQuery(id+"F6.imprint","IMPRINT",EDGE,{"derivedFrom":subQ14}),-1.0]])]});}
            extrude(context, id + "F7", {"entities" : qUnion([Q0]), "operationType" : NewBodyOperationType.REMOVE, "oppositeDirection" : true, "depth" : 617.22 * mm});
        }
        {
            var Q0;
            Q0=qCreatedBy(makeId("Right.planeOp"),FACE);
            var sketch = newSketch(context, id + "F8", { "sketchPlane" : qUnion([Q0])});
            skFitSpline(sketch, "E33", {"points": [v(278.97, 437.84) * mm, v(239.7, 546.9) * mm, v(216.44, 666.14) * mm, v(214.99, 762.12) * mm, v(212.08, 791.2) * mm, v(185.9, 802.83) * mm, v(162.64, 786.84) * mm, v(114.65, 475.65) * mm, v(121.92, 446.56) * mm, v(180.09, 346.23) * mm, v(201.9, 350.59) * mm, v(278.97, 437.84) * mm]});
            skFitSpline(sketch, "E34", {"points": [v(178.15, -355.19) * mm, v(211.05, -215.34) * mm, v(256.3, -48.77) * mm, v(298.84, 138.5) * mm, v(315.3, 306.1) * mm, v(308.1, 346.2) * mm, v(289.59, 348.26) * mm, v(227.9, 282.45) * mm, v(213.5, 254.69) * mm, v(142.55, -313.93) * mm], "startDerivative": vector(260.8, 1163.28) * mm, "endDerivative": vector(-357.18, -3242.65) * mm});
            skFitSpline(sketch, "E35", {"points": [v(178.15, -355.19) * mm, v(142.55, -313.93) * mm, v(88.15, -248.93) * mm, v(59.04, -211.08) * mm], "startDerivative": vector(-104.4, 120.4) * mm, "endDerivative": vector(-88.09, 117.81) * mm});
            skFitSpline(sketch, "E36", {"points": [v(88.15, -248.93) * mm, v(157.06, 256.72) * mm, v(156.1, 292.63) * mm, v(124.84, 337.91) * mm, v(112.58, 347.17) * mm, v(104.41, 330.29) * mm, v(84.68, 77.24) * mm, v(59.04, -211.08) * mm], "startDerivative": vector(302.64, 2248.83) * mm, "endDerivative": vector(-126.04, -1237.86) * mm});
            skLineSegment(sketch, "E37", {"start": v(170.59, -675.29) * mm, "end": v(170.59, -606.61) * mm});
            skLineSegment(sketch, "E38", {"start": v(156.62, -598.2) * mm, "end": v(130.78, -611.83) * mm});
            skLineSegment(sketch, "E39", {"start": v(125.7, -620.26) * mm, "end": v(125.7, -688.93) * mm});
            skLineSegment(sketch, "E40", {"start": v(139.68, -697.35) * mm, "end": v(165.51, -683.71) * mm});
            skLineSegment(sketch, "E41", {"start": v(91.74, -602.48) * mm, "end": v(91.74, -704.81) * mm});
            skLineSegment(sketch, "E42", {"start": v(86.66, -713.24) * mm, "end": v(57.67, -728.55) * mm});
            skLineSegment(sketch, "E43", {"start": v(43.7, -720.12) * mm, "end": v(43.7, -617.79) * mm});
            skLineSegment(sketch, "E44", {"start": v(48.77, -609.36) * mm, "end": v(77.77, -594.05) * mm});
            skPoint(sketch, "E45.visualSharp", {"position": v(170.59, -681.03) * mm});
            skArc(sketch, "E45.filletArc", {"start": v(165.51, -683.71) * mm, "mid": v(169.22, -680.2) * mm, "end": v(170.59, -675.29) * mm});
            skPoint(sketch, "E46.visualSharp", {"position": v(125.7, -614.51) * mm});
            skArc(sketch, "E46.filletArc", {"start": v(130.78, -611.83) * mm, "mid": v(127.07, -615.34) * mm, "end": v(125.7, -620.26) * mm});
            skPoint(sketch, "E47.visualSharp", {"position": v(125.7, -704.73) * mm});
            skArc(sketch, "E47.filletArc", {"start": v(125.7, -688.93) * mm, "mid": v(130.32, -697.09) * mm, "end": v(139.68, -697.35) * mm});
            skPoint(sketch, "E48.visualSharp", {"position": v(170.59, -590.81) * mm});
            skArc(sketch, "E48.filletArc", {"start": v(170.59, -606.61) * mm, "mid": v(165.98, -598.46) * mm, "end": v(156.62, -598.2) * mm});
            skPoint(sketch, "E49.visualSharp", {"position": v(43.7, -735.92) * mm});
            skArc(sketch, "E49.filletArc", {"start": v(43.7, -720.12) * mm, "mid": v(48.3, -728.28) * mm, "end": v(57.67, -728.55) * mm});
            skPoint(sketch, "E50.visualSharp", {"position": v(91.74, -586.68) * mm});
            skArc(sketch, "E50.filletArc", {"start": v(91.74, -602.48) * mm, "mid": v(87.13, -594.32) * mm, "end": v(77.77, -594.05) * mm});
            skPoint(sketch, "E51.visualSharp", {"position": v(91.74, -710.55) * mm});
            skArc(sketch, "E51.filletArc", {"start": v(86.66, -713.24) * mm, "mid": v(90.37, -709.73) * mm, "end": v(91.74, -704.81) * mm});
            skPoint(sketch, "E52.visualSharp", {"position": v(43.7, -612.05) * mm});
            skArc(sketch, "E52.filletArc", {"start": v(48.77, -609.36) * mm, "mid": v(45.06, -612.87) * mm, "end": v(43.7, -617.79) * mm});
            skSolve(sketch);
        }
        {
            var Q0;
            Q0 = qSketchRegion(id + "F8", true);
            extrude(context, id + "F9", {"entities" : qUnion([Q0]), "operationType" : NewBodyOperationType.REMOVE, "endBound" : BoundingType.THROUGH_ALL, "oppositeDirection" : true, "depth" : 25.4 * mm, "hasSecondDirection" : true, "secondDirectionBound" : SecondDirectionBoundingType.THROUGH_ALL, "secondDirectionOppositeDirection" : false, "secondDirectionDepth" : 25.4 * mm});
        }
    });
